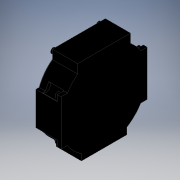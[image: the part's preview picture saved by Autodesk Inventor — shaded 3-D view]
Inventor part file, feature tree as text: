
AUTODESK INVENTOR PART (.ipt)
format: ipt  version: 2019 (Build 230136000, 136)  size: 310,784 bytes
history: native  units: mm
features: other x21, extrude x18, sketch x18
ambient origin geometry x8: Origin, YZ Plane, XZ Plane, XY Plane, X Axis, Y Axis, Z Axis, Center Point
bodies: Solid1 (feature_tree)
feature tree (57):
  extrude  "Extrusion1"  Depth=7.9mm TaperAngle=0.0deg
  extrude  "Extrusion2"  Depth=5.0mm TaperAngle=0.0deg
  extrude  "Extrusion3"  Depth=20.0mm TaperAngle=0.0deg
  extrude  "Extrusion4"  Depth=20.0mm TaperAngle=0.0deg
  extrude  "Extrusion5"  Depth=3.5mm TaperAngle=0.0deg
  extrude  "Extrusion6"  Depth=3.5mm TaperAngle=0.0deg
  extrude  "Extrusion7"  Depth=5.0mm TaperAngle=0.0deg
  extrude  "Extrusion8"  Depth=5.0mm TaperAngle=0.0deg
  extrude  "Extrusion9"  Depth=0.5mm TaperAngle=0.0deg
  extrude  "Extrusion10"  [1 undecoded]
  extrude  "Extrusion11"  [1 undecoded]
  extrude  "Extrusion12"  [1 undecoded]
  extrude  "Extrusion13"  [1 undecoded]
  extrude  "Extrusion14"  [1 undecoded]
  extrude  "Extrusion15"  [1 undecoded]
  extrude  "Extrusion16"  [1 undecoded]
  extrude  "Extrusion17"  [1 undecoded]
  extrude  "Extrusion18"  [1 undecoded]
  other  "CON1_XY"
  other  "CON1_YZ"
  other  "CON1_ZX"
  other  "CON1_X"
  other  "CON1_Y"
  other  "CON1_Z"
  other  "CON1_Center"
  other  "CON2_XY"
  other  "CON2_YZ"
  other  "CON2_ZX"
  other  "CON2_X"
  other  "CON2_Y"
  other  "CON2_Z"
  other  "CON2_Center"
  other  "R_XY"
  other  "R_YZ"
  other  "R_ZX"
  other  "R_X"
  other  "R_Y"
  other  "R_Z"
  other  "R_Center"
  sketch  "Sketch_1"  dims[d0=29.4mm d1=0.0mm d2=7.9mm d3=0.0mm]
  sketch  "Sketch_2"  dims[d4=5.0mm d5=0.0mm d6=1.0mm d7=0.0mm]
  sketch  "Sketch_3"  dims[d8=20.0mm d9=0.0mm d10=20.0mm d11=0.0mm]
  sketch  "Sketch_7"  dims[d24=3.9mm d25=0.0mm d26=5.0mm d27=0.0mm]
  sketch  "Sketch_8"  dims[d28=5.0mm d29=0.0mm d30=5.0mm d31=0.0mm]
  sketch  "Sketch_9"  dims[d32=5.0mm d33=0.0mm d34=0.5mm d35=0.0mm]
  sketch  "Sketch_10"  dims[d36=0.0mm d37=0.0mm d38=0.0mm]
  sketch  "Sketch_11"
  sketch  "Sketch_12"
  sketch  "Sketch_13"
  sketch  "Sketch_14"
  sketch  "Sketch_15"
  sketch  "Sketch_21"
  sketch  "Sketch_22"
  sketch  "Sketch_4"  dims[d12=20.0mm d13=0.0mm d14=20.0mm d15=0.0mm]
  sketch  "Sketch_5"  dims[d16=3.5mm d17=0.0mm d18=3.5mm d19=0.0mm]
  sketch  "Sketch_6"  dims[d20=3.5mm d21=0.0mm d22=3.5mm d23=0.0mm]
  sketch  "Sketch_24"
note: 9 required parameter values undecoded (feature->parameter linkage not recoverable at this tier; creation-order binding heuristic only, values carry confidence <= 0.55)
